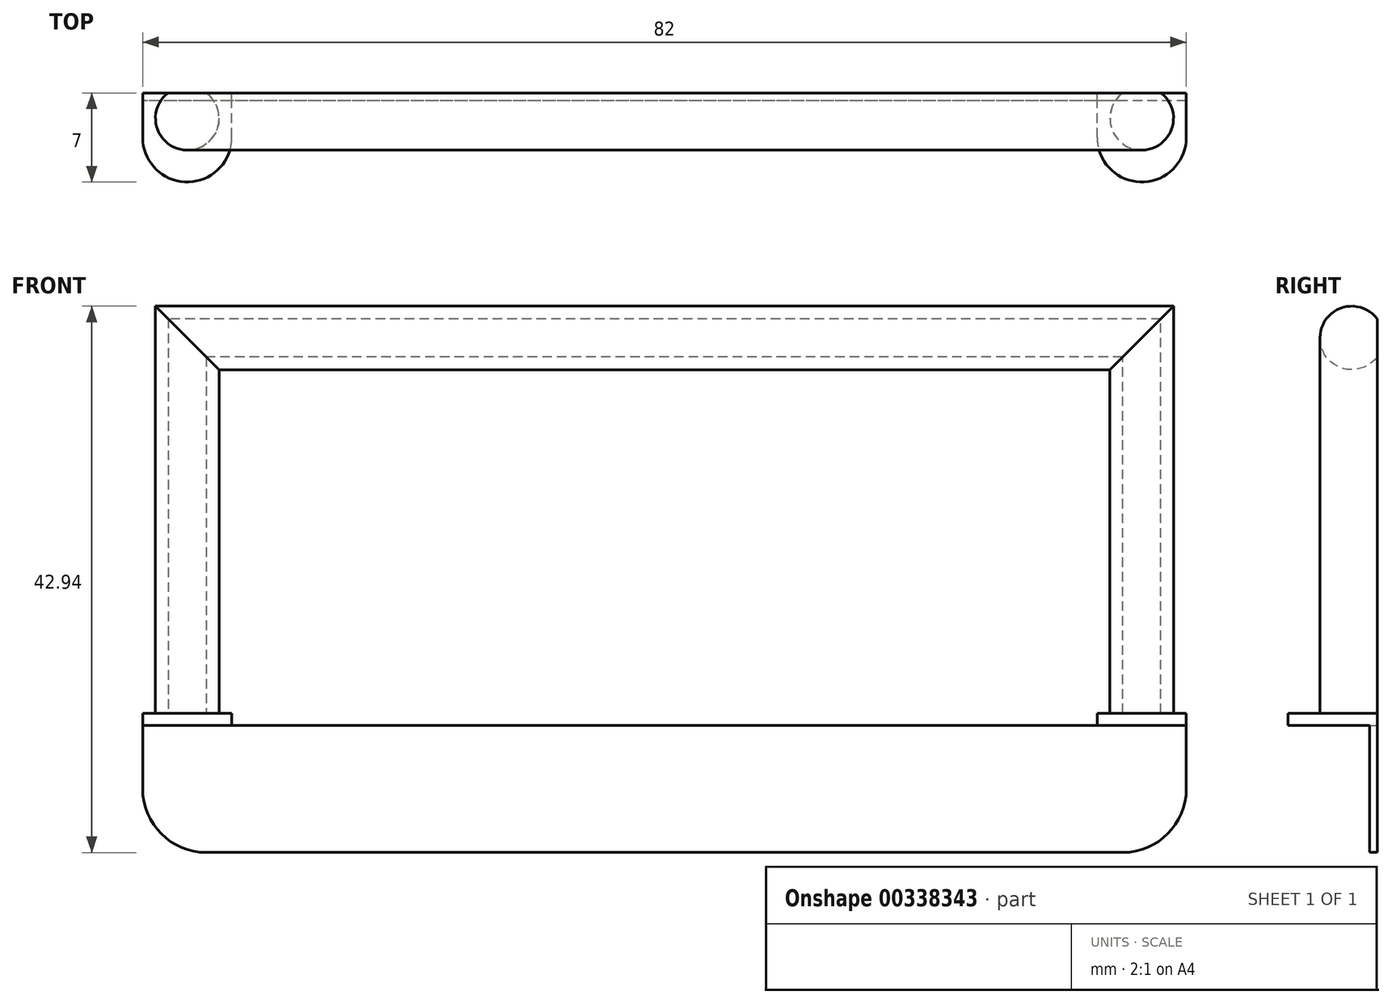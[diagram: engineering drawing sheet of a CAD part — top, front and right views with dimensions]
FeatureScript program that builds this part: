
annotation { "Feature Type Name" : "Feature", "Feature Type Description" : "" }
export const myFeature = defineFeature(function(context is Context, id is Id, definition is map)
    precondition{}
    {
        {
            assignVariable(context, id + "F0", {"name" : "diameter", "anyValue" : 5});
        }
        {
            var Q0;
            Q0=qCreatedBy(makeId("Front.planeOp"),FACE);
            var sketch = newSketch(context, id + "F1", { "sketchPlane" : qUnion([Q0])});
            skLineSegment(sketch, "E0", {"start": v(-40, 0) * mm, "end": v(-40, 32) * mm});
            skLineSegment(sketch, "E1", {"start": v(-40, 32) * mm, "end": v(40, 32) * mm});
            skLineSegment(sketch, "E2", {"start": v(40, 32) * mm, "end": v(40, 0) * mm});
            skLineSegment(sketch, "E3.0", {"start": v(35, 27) * mm, "end": v(35, 0) * mm});
            skLineSegment(sketch, "E3.1", {"start": v(-35, 27) * mm, "end": v(35, 27) * mm});
            skLineSegment(sketch, "E3.2", {"start": v(-35, 0) * mm, "end": v(-35, 27) * mm});
            skLineSegment(sketch, "E4", {"start": v(-40, 0) * mm, "end": v(-35, 0) * mm});
            skLineSegment(sketch, "E5", {"start": v(35, 0) * mm, "end": v(40, 0) * mm});
            skSolve(sketch);
        }
        {
            var Q0;
            Q0=makeQuery(id+"F1.imprint","IMPRINT",FACE,{"disambiguationData":[TD([[makeQuery(id+"F1.imprint","IMPRINT",EDGE,{"derivedFrom":sQuery(id+"F1.wireOp",EDGE,"E0")}),-1.0]])]});
            extrude(context, id + "F2", {"entities" : qUnion([Q0]), "depth" : (getVariable(context, 'diameter')) * mm});
        }
        {
            var Q0;
            Q0=makeQuery(id+"F2.opExtrude","CAP_EDGE",EDGE,{"disambiguationData":[OSD([sQuery(id+"F1.wireOp",EDGE,"E3.2")])],"isStart":false});
            var Q1;
            Q1=makeQuery(id+"F2.opExtrude","CAP_EDGE",EDGE,{"disambiguationData":[OSD([sQuery(id+"F1.wireOp",EDGE,"E3.2")])],"isStart":true});
            var Q2;
            Q2=makeQuery(id+"F2.opExtrude","CAP_EDGE",EDGE,{"disambiguationData":[OSD([sQuery(id+"F1.wireOp",EDGE,"E2")])],"isStart":false});
            var Q3;
            Q3=makeQuery(id+"F2.opExtrude","CAP_EDGE",EDGE,{"disambiguationData":[OSD([sQuery(id+"F1.wireOp",EDGE,"E2")])],"isStart":true});
            var Q4;
            Q4=makeQuery(id+"F2.opExtrude","CAP_EDGE",EDGE,{"disambiguationData":[OSD([sQuery(id+"F1.wireOp",EDGE,"E3.0")])],"isStart":false});
            var Q5;
            Q5=makeQuery(id+"F2.opExtrude","CAP_EDGE",EDGE,{"disambiguationData":[OSD([sQuery(id+"F1.wireOp",EDGE,"E3.0")])],"isStart":true});
            var Q6;
            Q6=makeQuery(id+"F2.opExtrude","CAP_EDGE",EDGE,{"disambiguationData":[OSD([sQuery(id+"F1.wireOp",EDGE,"E3.1")])],"isStart":true});
            var Q7;
            Q7=makeQuery(id+"F2.opExtrude","CAP_EDGE",EDGE,{"disambiguationData":[OSD([sQuery(id+"F1.wireOp",EDGE,"E1")])],"isStart":true});
            var Q8;
            Q8=makeQuery(id+"F2.opExtrude","CAP_EDGE",EDGE,{"disambiguationData":[OSD([sQuery(id+"F1.wireOp",EDGE,"E0")])],"isStart":true});
            var Q9;
            Q9=makeQuery(id+"F2.opExtrude","CAP_EDGE",EDGE,{"disambiguationData":[OSD([sQuery(id+"F1.wireOp",EDGE,"E1")])],"isStart":false});
            var Q10;
            Q10=makeQuery(id+"F2.opExtrude","CAP_EDGE",EDGE,{"disambiguationData":[OSD([sQuery(id+"F1.wireOp",EDGE,"E0")])],"isStart":false});
            var Q11;
            Q11=makeQuery(id+"F2.opExtrude","CAP_EDGE",EDGE,{"disambiguationData":[OSD([sQuery(id+"F1.wireOp",EDGE,"E3.1")])],"isStart":false});
            fillet(context, id + "F3", {"entities" : qUnion([Q0, Q1, Q2, Q3, Q4, Q5, Q6, Q7, Q8, Q9, Q10, Q11]), "radius" : (getVariable(context, 'diameter') / 2) * mm, "tangentPropagation" : true, "allowEdgeOverflow" : false});
        }
        {
            var Q0;
            Q0=qCreatedBy(makeId("Front.planeOp"),FACE);
            var sketch = newSketch(context, id + "F4", { "sketchPlane" : qUnion([Q0])});
            skLineSegment(sketch, "E6.0", {"start": v(-35, 0) * mm, "end": v(-40, 0) * mm, "construction": true});
            skLineSegment(sketch, "E6.1", {"start": v(-35, 27) * mm, "end": v(-40, 32) * mm, "construction": true});
            skLineSegment(sketch, "E6.2", {"start": v(40, 0) * mm, "end": v(35, 0) * mm, "construction": true});
            skLineSegment(sketch, "E6.3", {"start": v(35, 27) * mm, "end": v(40, 32) * mm, "construction": true});
            skLineSegment(sketch, "E7.bottom", {"start": v(-40, 32) * mm, "end": v(40, 32) * mm});
            skLineSegment(sketch, "E7.top", {"start": v(-40, 0) * mm, "end": v(40, 0) * mm});
            skLineSegment(sketch, "E7.left", {"start": v(-40, 32) * mm, "end": v(-40, 0) * mm});
            skLineSegment(sketch, "E7.right", {"start": v(40, 32) * mm, "end": v(40, 0) * mm});
            skSolve(sketch);
        }
        {
            var Q0;
            Q0=makeQuery(id+"F4.imprint","IMPRINT",FACE,{"disambiguationData":[TD([[makeQuery(id+"F4.imprint","IMPRINT",EDGE,{"derivedFrom":sQuery(id+"F4.wireOp",EDGE,"E7.bottom")}),-1.0]])]});
            extrude(context, id + "F5", {"entities" : qUnion([Q0]), "operationType" : NewBodyOperationType.REMOVE, "depth" : (getVariable(context, 'diameter') / 10) * mm});
        }
        {
            var Q0;
            Q0=makeQuery(id+"F5.boolean.opBoolean","COPY",FACE,{"derivedFrom":makeQuery(id+"F5.opExtrude","CAP_FACE",FACE,{"disambiguationData":[OSD([sQuery(id+"F4.wireOp",EDGE,"E7.bottom"),sQuery(id+"F4.wireOp",EDGE,"E7.top"),sQuery(id+"F4.wireOp",EDGE,"E7.left"),sQuery(id+"F4.wireOp",EDGE,"E7.right")])],"isStart":false})});
            var sketch = newSketch(context, id + "F6", { "sketchPlane" : qUnion([Q0])});
            skLineSegment(sketch, "E8", {"start": v(-37.5, 0) * mm, "end": v(-41, 0) * mm});
            skPoint(sketch, "E8.endSnap0", {"position": v(-37.5, 0) * mm});
            skLineSegment(sketch, "E9", {"start": v(-41, 0) * mm, "end": v(-41, -0.94) * mm});
            skLineSegment(sketch, "E10", {"start": v(-41, -0.94) * mm, "end": v(-41, -10.94) * mm});
            skLineSegment(sketch, "E11", {"start": v(-41, -10.94) * mm, "end": v(0, -10.94) * mm});
            skLineSegment(sketch, "E12", {"start": v(-37.5, 0) * mm, "end": v(-34, 0) * mm});
            skLineSegment(sketch, "E13", {"start": v(-34, 0) * mm, "end": v(-34, -0.94) * mm});
            skLineSegment(sketch, "E14", {"start": v(-34, -0.94) * mm, "end": v(-41, -0.94) * mm});
            skLineSegment(sketch, "E15", {"start": v(-34, -0.94) * mm, "end": v(0, -0.94) * mm});
            skLineSegment(sketch, "E16.MirrorCS", {"start": v(41, 0) * mm, "end": v(41, -0.94) * mm});
            skLineSegment(sketch, "E17.MirrorCS", {"start": v(37.5, 0) * mm, "end": v(41, 0) * mm});
            skLineSegment(sketch, "E18.MirrorCS", {"start": v(37.5, 0) * mm, "end": v(34, 0) * mm});
            skLineSegment(sketch, "E19.MirrorCS", {"start": v(34, 0) * mm, "end": v(34, -0.94) * mm});
            skLineSegment(sketch, "E20.MirrorCS", {"start": v(34, -0.94) * mm, "end": v(41, -0.94) * mm});
            skLineSegment(sketch, "E21.MirrorCS", {"start": v(41, -0.94) * mm, "end": v(41, -10.94) * mm});
            skLineSegment(sketch, "E22.MirrorCS", {"start": v(41, -10.94) * mm, "end": v(0, -10.94) * mm});
            skLineSegment(sketch, "E23.MirrorCS", {"start": v(34, -0.94) * mm, "end": v(0, -0.94) * mm});
            skSolve(sketch);
        }
        {
            var Q0;
            {var subQ0=sQuery(id+"F6.wireOp",EDGE,"E9");Q0=makeQuery(id+"F6.imprint","IMPRINT",FACE,{"disambiguationData":[TD([[makeQuery(id+"F6.imprint","IMPRINT",EDGE,{"derivedFrom":subQ0}),1.0]])]});}
            var Q1;
            {var subQ7=sQuery(id+"F6.wireOp",EDGE,"E16.MirrorCS");Q1=makeQuery(id+"F6.imprint","IMPRINT",FACE,{"disambiguationData":[TD([[makeQuery(id+"F6.imprint","IMPRINT",EDGE,{"derivedFrom":subQ7}),-1.0]])]});}
            extrude(context, id + "F7", {"entities" : qUnion([Q0, Q1]), "operationType" : NewBodyOperationType.ADD, "oppositeDirection" : true, "depth" : (getVariable(context, 'diameter') + 2) * mm});
        }
        {
            var Q0;
            Q0=makeQuery(id+"F6.imprint","IMPRINT",FACE,{"disambiguationData":[TD([[makeQuery(id+"F6.imprint","IMPRINT",EDGE,{"derivedFrom":sQuery(id+"F6.wireOp",EDGE,"E10")}),1.0]])]});
            extrude(context, id + "F8", {"entities" : qUnion([Q0]), "operationType" : NewBodyOperationType.ADD, "oppositeDirection" : true, "depth" : 0.6 * mm});
        }
        {
            var Q0;
            Q0=makeQuery(id+"F7.opExtrude","CAP_EDGE",EDGE,{"disambiguationData":[OSD([sQuery(id+"F6.wireOp",EDGE,"E9")])],"isStart":false});
            var Q1;
            Q1=makeQuery(id+"F7.opExtrude","CAP_EDGE",EDGE,{"disambiguationData":[OSD([sQuery(id+"F6.wireOp",EDGE,"E13")])],"isStart":false});
            var Q2;
            Q2=makeQuery(id+"F7.opExtrude","CAP_EDGE",EDGE,{"disambiguationData":[OSD([sQuery(id+"F6.wireOp",EDGE,"E19.MirrorCS")])],"isStart":false});
            var Q3;
            Q3=makeQuery(id+"F7.opExtrude","CAP_EDGE",EDGE,{"disambiguationData":[OSD([sQuery(id+"F6.wireOp",EDGE,"E16.MirrorCS")])],"isStart":false});
            fillet(context, id + "F9", {"entities" : qUnion([Q0, Q1, Q2, Q3]), "radius" : ((getVariable(context, 'diameter') + 2) / 2) * mm, "tangentPropagation" : true, "allowEdgeOverflow" : false});
        }
        {
            var Q0;
            Q0=makeQuery(id+"F8.opExtrude","SWEPT_EDGE",EDGE,{"disambiguationData":[OSD([sQuery(id+"F6.wireOp",EDGE,"E10"),sQuery(id+"F6.wireOp",EDGE,"E11")])]});
            var Q1;
            Q1=makeQuery(id+"F8.opExtrude","SWEPT_EDGE",EDGE,{"disambiguationData":[OSD([sQuery(id+"F6.wireOp",EDGE,"E21.MirrorCS"),sQuery(id+"F6.wireOp",EDGE,"E22.MirrorCS")])]});
            fillet(context, id + "F10", {"entities" : qUnion([Q0, Q1]), "radius" : 5 * mm, "tangentPropagation" : true, "allowEdgeOverflow" : false});
        }
    });
